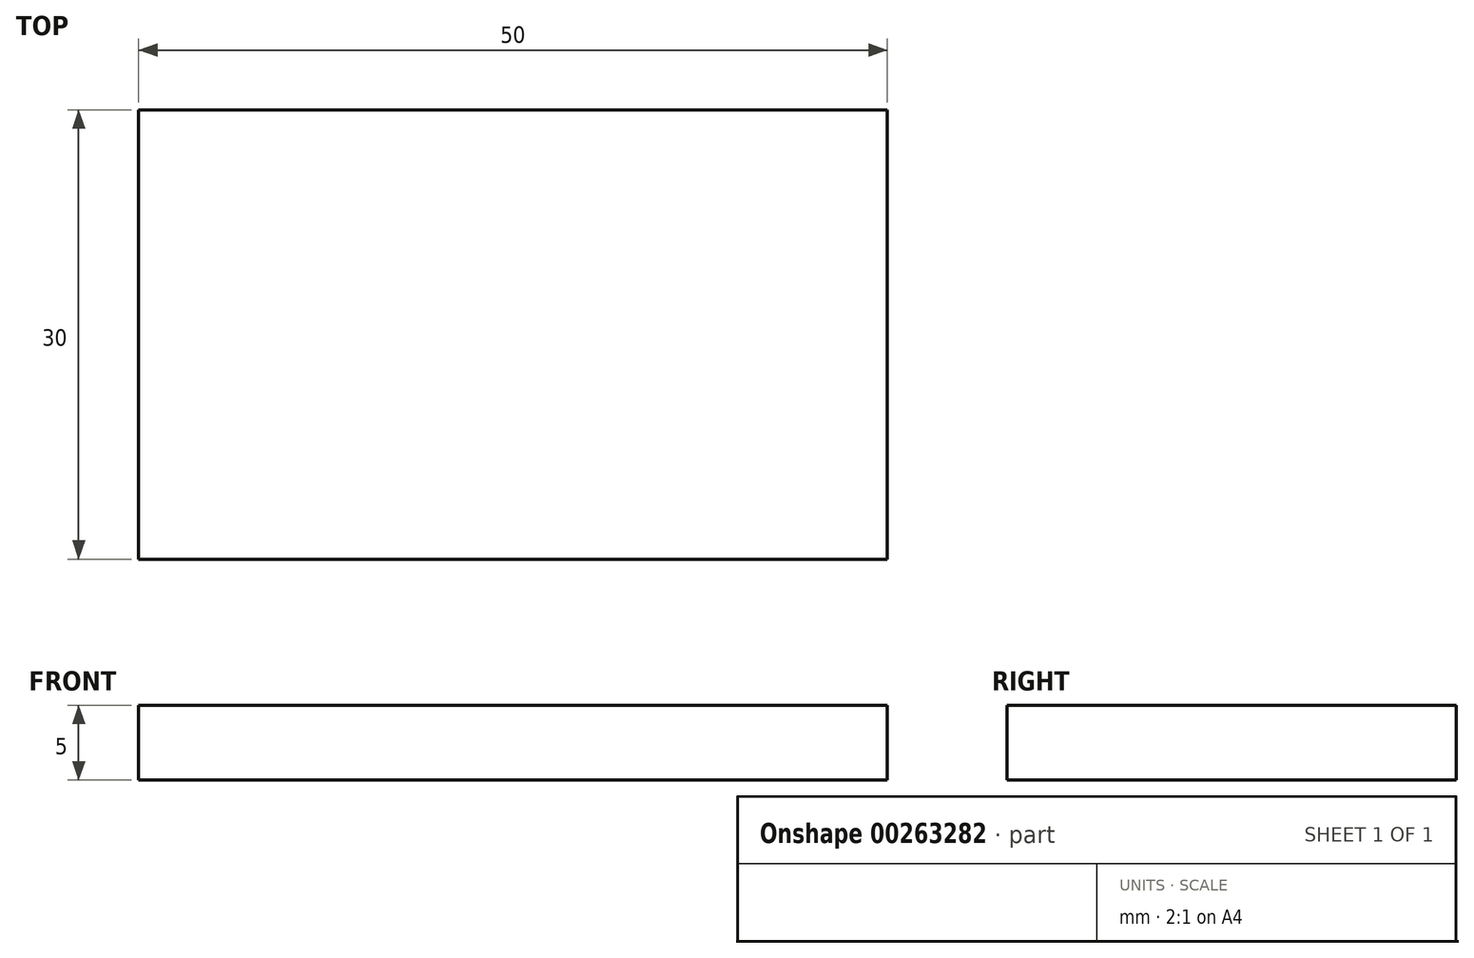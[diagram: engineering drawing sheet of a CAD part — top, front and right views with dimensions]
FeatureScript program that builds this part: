
annotation { "Feature Type Name" : "Feature", "Feature Type Description" : "" }
export const myFeature = defineFeature(function(context is Context, id is Id, definition is map)
    precondition{}
    {
        {
            var Q0;
            Q0=qCreatedBy(makeId("Front.planeOp"),FACE);
            var sketch = newSketch(context, id + "F0", { "sketchPlane" : qUnion([Q0])});
            skLineSegment(sketch, "E0.bottom", {"start": v(25, -2.5) * mm, "end": v(-25, -2.5) * mm});
            skLineSegment(sketch, "E0.top", {"start": v(25, 2.5) * mm, "end": v(-25, 2.5) * mm});
            skLineSegment(sketch, "E0.left", {"start": v(25, -2.5) * mm, "end": v(25, 2.5) * mm});
            skLineSegment(sketch, "E0.right", {"start": v(-25, -2.5) * mm, "end": v(-25, 2.5) * mm});
            skPoint(sketch, "E0.middle", {"position": v(0, 0) * mm});
            skSolve(sketch);
        }
        {
            var Q0;
            Q0 = qSketchRegion(id + "F0", true);
            extrude(context, id + "F1", {"entities" : qUnion([Q0]), "depth" : 30 * mm});
        }
    });
